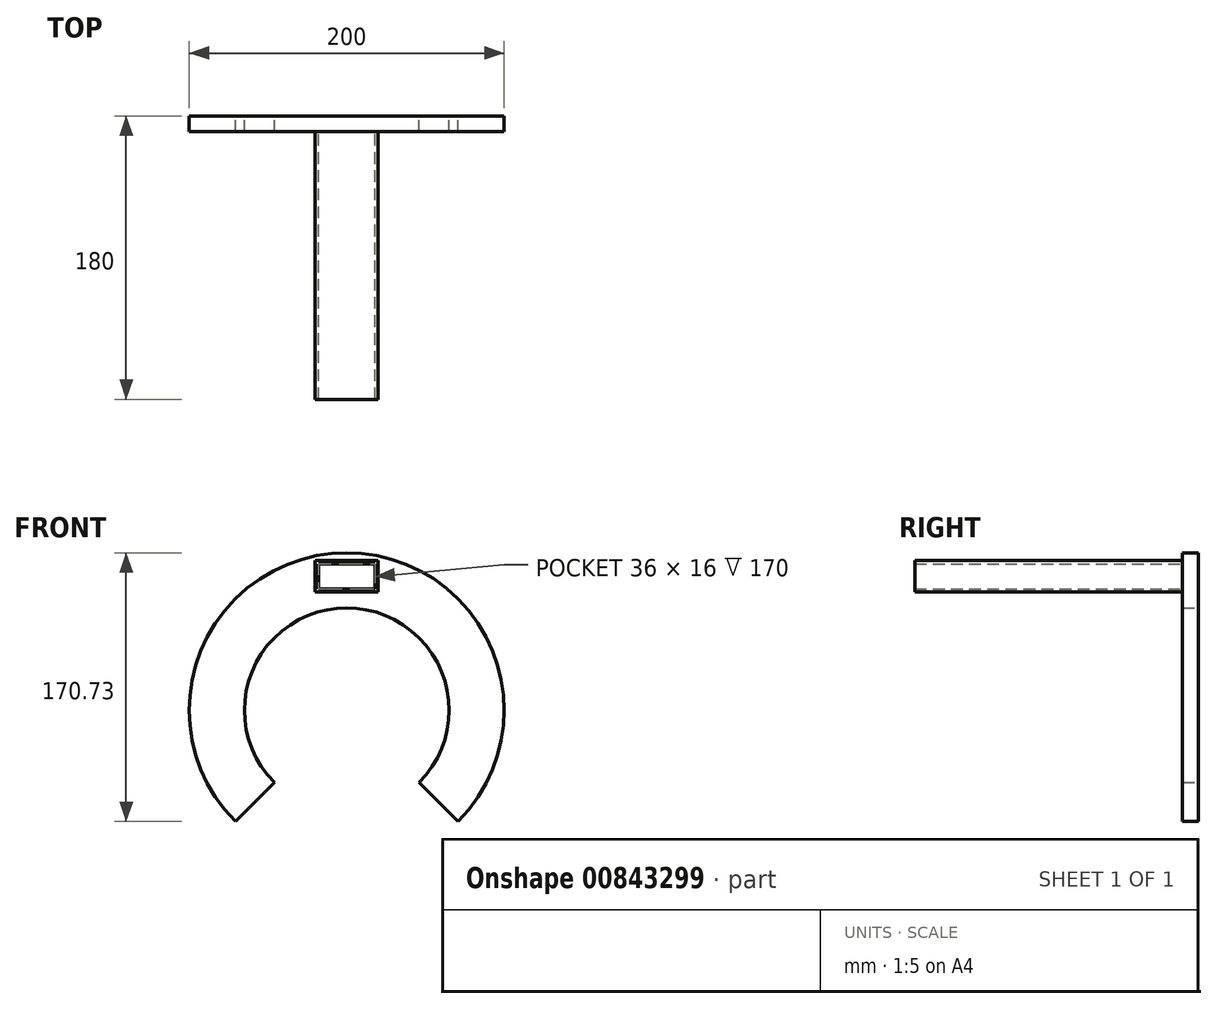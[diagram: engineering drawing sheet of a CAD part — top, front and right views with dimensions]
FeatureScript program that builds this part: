
annotation { "Feature Type Name" : "Feature", "Feature Type Description" : "" }
export const myFeature = defineFeature(function(context is Context, id is Id, definition is map)
    precondition{}
    {
        {
            var Q0;
            Q0=qCreatedBy(makeId("Front.planeOp"),FACE);
            var sketch = newSketch(context, id + "F0", { "sketchPlane" : qUnion([Q0])});
            skArc(sketch, "E0", {"start": v(70.73, -70.7) * mm, "mid": v(-0.03, 100) * mm, "end": v(-70.7, -70.73) * mm});
            skArc(sketch, "E1", {"start": v(45.98, -45.95) * mm, "mid": v(-0.02, 65) * mm, "end": v(-45.95, -45.98) * mm});
            skLineSegment(sketch, "E2", {"start": v(0, 0) * mm, "end": v(-70.7, -70.73) * mm});
            skLineSegment(sketch, "E3", {"start": v(0, 0) * mm, "end": v(70.73, -70.7) * mm});
            skSolve(sketch);
        }
        {
            var Q0;
            {var subQ0=sQuery(id+"F0.wireOp",EDGE,"E0");Q0=makeQuery(id+"F0.imprint","IMPRINT",FACE,{"disambiguationData":[TD([[makeQuery(id+"F0.imprint","IMPRINT",EDGE,{"derivedFrom":subQ0}),1.0]])]});}
            extrude(context, id + "F1", {"entities" : qUnion([Q0]), "depth" : 10 * mm, "offsetDistance" : 25 * mm});
        }
        {
            var Q0;
            Q0=qCreatedBy(makeId("Front.planeOp"),FACE);
            var sketch = newSketch(context, id + "F2", { "sketchPlane" : qUnion([Q0])});
            skLineSegment(sketch, "E4.bottom", {"start": v(-20, 95) * mm, "end": v(20, 95) * mm});
            skLineSegment(sketch, "E4.top", {"start": v(-20, 75) * mm, "end": v(20, 75) * mm});
            skLineSegment(sketch, "E4.left", {"start": v(-20, 95) * mm, "end": v(-20, 75) * mm});
            skLineSegment(sketch, "E4.right", {"start": v(20, 95) * mm, "end": v(20, 75) * mm});
            skLineSegment(sketch, "E5.bottom", {"start": v(-18, 93) * mm, "end": v(18, 93) * mm});
            skLineSegment(sketch, "E5.top", {"start": v(-18, 77) * mm, "end": v(18, 77) * mm});
            skLineSegment(sketch, "E5.left", {"start": v(-18, 93) * mm, "end": v(-18, 77) * mm});
            skLineSegment(sketch, "E5.right", {"start": v(18, 93) * mm, "end": v(18, 77) * mm});
            skSolve(sketch);
        }
        {
            var Q0;
            Q0 = qSketchRegion(id + "F2", true);
            extrude(context, id + "F3", {"entities" : qUnion([Q0]), "operationType" : NewBodyOperationType.ADD, "depth" : 180 * mm, "offsetDistance" : 25 * mm});
        }
    });
